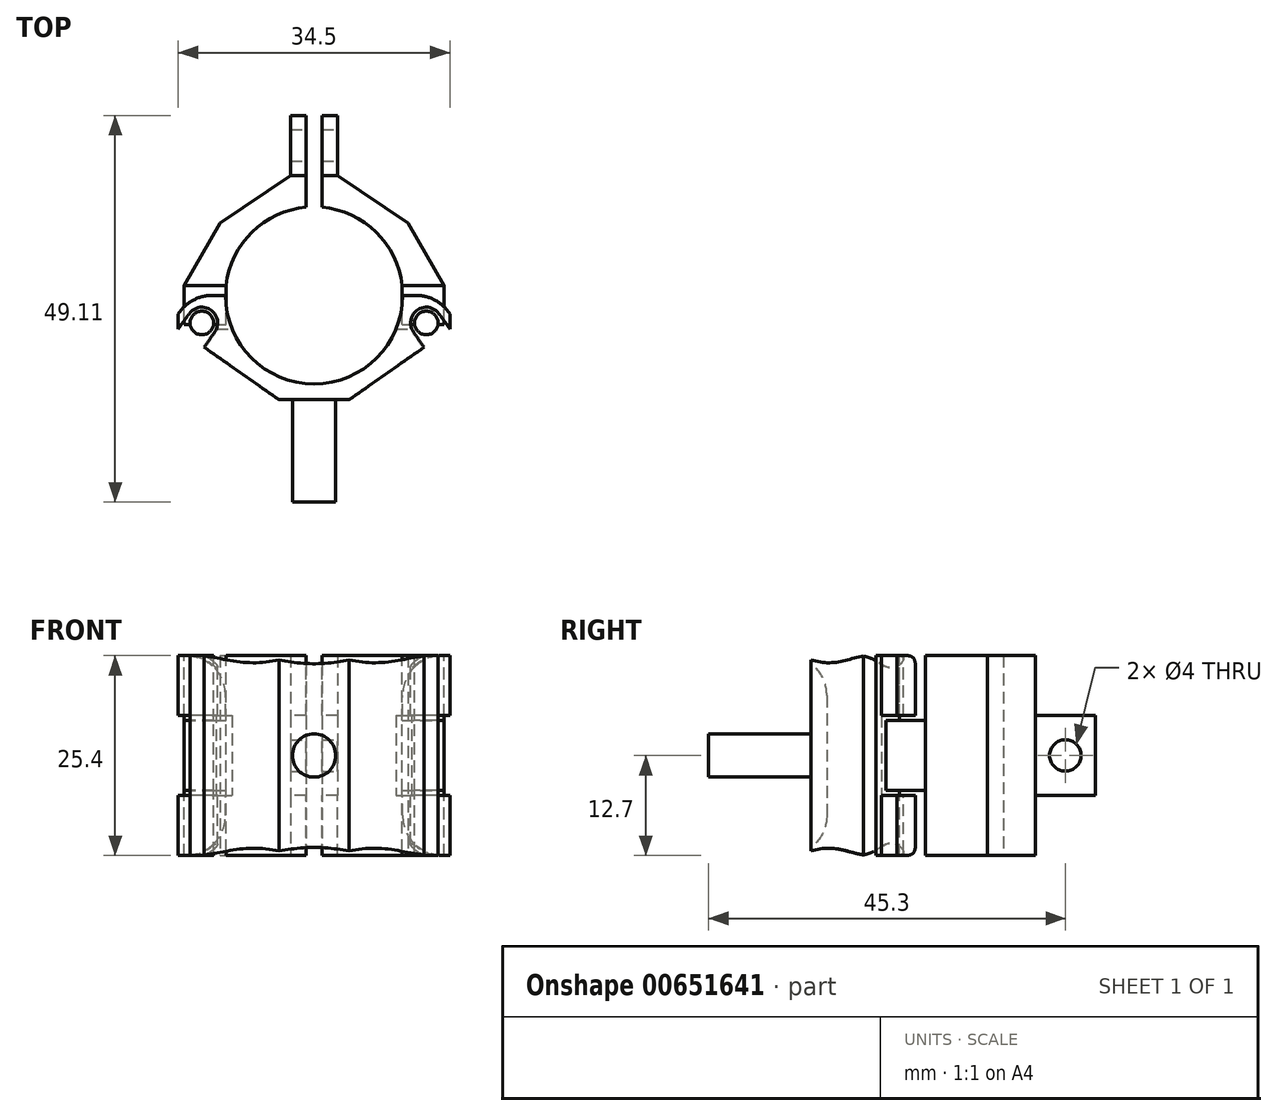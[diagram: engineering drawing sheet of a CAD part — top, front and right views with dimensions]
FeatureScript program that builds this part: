
annotation { "Feature Type Name" : "Feature", "Feature Type Description" : "" }
export const myFeature = defineFeature(function(context is Context, id is Id, definition is map)
    precondition{}
    {
        {
            var Q0;
            Q0=qCreatedBy(makeId("Top.planeOp"),FACE);
            var sketch = newSketch(context, id + "F0", { "sketchPlane" : qUnion([Q0])});
            skCircle(sketch, "E0", {"center": v(0, 0) * mm, "radius": 11.25 * mm});
            skLineSegment(sketch, "E1.bottom", {"start": v(-17.25, 0) * mm, "end": v(17.25, 0) * mm});
            skLineSegment(sketch, "E1.top", {"start": v(-17.25, -13.25) * mm, "end": v(17.25, -13.25) * mm});
            skLineSegment(sketch, "E1.left", {"start": v(-17.25, 0) * mm, "end": v(-17.25, -13.25) * mm});
            skLineSegment(sketch, "E1.right", {"start": v(17.25, 0) * mm, "end": v(17.25, -13.25) * mm});
            skLineSegment(sketch, "E2", {"start": v(-17.25, 0) * mm, "end": v(-11.95, 9.17) * mm});
            skLineSegment(sketch, "E3", {"start": v(-11.95, 9.17) * mm, "end": v(-3, 15.24) * mm});
            skLineSegment(sketch, "E4", {"start": v(17.25, 0) * mm, "end": v(11.95, 9.17) * mm});
            skLineSegment(sketch, "E5", {"start": v(11.95, 9.17) * mm, "end": v(3, 15.24) * mm});
            skLineSegment(sketch, "E6", {"start": v(-3, 15.24) * mm, "end": v(-3, 22.86) * mm});
            skLineSegment(sketch, "E7", {"start": v(-3, 22.86) * mm, "end": v(-1, 22.86) * mm});
            skLineSegment(sketch, "E8", {"start": v(-1, 22.86) * mm, "end": v(-1, 11.2) * mm});
            skLineSegment(sketch, "E9", {"start": v(3, 15.24) * mm, "end": v(3, 22.86) * mm});
            skLineSegment(sketch, "E10", {"start": v(3, 22.86) * mm, "end": v(1, 22.86) * mm});
            skLineSegment(sketch, "E11", {"start": v(1, 22.86) * mm, "end": v(1, 11.2) * mm});
            skSolve(sketch);
        }
        {
            var Q0;
            {var subQ0=sQuery(id+"F0.wireOp",EDGE,"E2");Q0=makeQuery(id+"F0.imprint","IMPRINT",FACE,{"disambiguationData":[TD([[makeQuery(id+"F0.imprint","IMPRINT",EDGE,{"derivedFrom":subQ0}),-1.0]])]});}
            var Q1;
            Q1=makeQuery(id+"F0.imprint","IMPRINT",FACE,{"disambiguationData":[TD([[makeQuery(id+"F0.imprint","IMPRINT",EDGE,{"derivedFrom":sQuery(id+"F0.wireOp",EDGE,"E1.top")}),1.0]])]});
            var Q2;
            {var subQ0=sQuery(id+"F0.wireOp",EDGE,"E4");Q2=makeQuery(id+"F0.imprint","IMPRINT",FACE,{"disambiguationData":[TD([[makeQuery(id+"F0.imprint","IMPRINT",EDGE,{"derivedFrom":subQ0}),1.0]])]});}
            extrude(context, id + "F1", {"entities" : qUnion([Q0, Q1, Q2]), "depth" : 25.4 * mm, "offsetDistance" : 25.4 * mm});
        }
        {
            var Q0;
            Q0=makeQuery(id+"F1.opExtrude","SWEPT_FACE",FACE,{"disambiguationData":[OSD([sQuery(id+"F0.wireOp",EDGE,"E9")])]});
            var sketch = newSketch(context, id + "F2", { "sketchPlane" : qUnion([Q0])});
            skCircle(sketch, "E12", {"center": v(19.05, 12.7) * mm, "radius": 2 * mm});
            skPoint(sketch, "E12.centerSnap0", {"position": v(22.86, 12.7) * mm});
            skPoint(sketch, "E12.centerSnap1", {"position": v(19.05, 25.4) * mm});
            skSolve(sketch);
        }
        {
            var Q0;
            Q0 = qSketchRegion(id + "F2", true);
            extrude(context, id + "F3", {"entities" : qUnion([Q0]), "operationType" : NewBodyOperationType.REMOVE, "oppositeDirection" : true, "depth" : 25.4 * mm, "offsetDistance" : 25.4 * mm});
        }
        {
            var Q0;
            Q0=makeQuery(id+"F1.opExtrude","SWEPT_FACE",FACE,{"disambiguationData":[OSD([sQuery(id+"F0.wireOp",EDGE,"E1.top")])]});
            var sketch = newSketch(context, id + "F4", { "sketchPlane" : qUnion([Q0])});
            skCircle(sketch, "E13", {"center": v(0, 12.7) * mm, "radius": 2.75 * mm});
            skPoint(sketch, "E13.centerSnap0", {"position": v(17.25, 12.7) * mm});
            skSolve(sketch);
        }
        {
            var Q0;
            Q0 = qSketchRegion(id + "F4", true);
            extrude(context, id + "F5", {"entities" : qUnion([Q0]), "operationType" : NewBodyOperationType.ADD, "depth" : 13 * mm, "offsetDistance" : 25.4 * mm});
        }
        {
            var Q0;
            Q0=makeQuery(id+"F1.opExtrude","CAP_FACE",FACE,{"disambiguationData":[OSD([sQuery(id+"F0.wireOp",EDGE,"E0"),sQuery(id+"F0.wireOp",EDGE,"E1.top"),sQuery(id+"F0.wireOp",EDGE,"E1.left"),sQuery(id+"F0.wireOp",EDGE,"E1.right"),sQuery(id+"F0.wireOp",EDGE,"E2"),sQuery(id+"F0.wireOp",EDGE,"E3"),sQuery(id+"F0.wireOp",EDGE,"E4"),sQuery(id+"F0.wireOp",EDGE,"E5"),sQuery(id+"F0.wireOp",EDGE,"E6"),sQuery(id+"F0.wireOp",EDGE,"E7"),sQuery(id+"F0.wireOp",EDGE,"E8"),sQuery(id+"F0.wireOp",EDGE,"E9"),sQuery(id+"F0.wireOp",EDGE,"E10"),sQuery(id+"F0.wireOp",EDGE,"E11")])],"isStart":false});
            var sketch = newSketch(context, id + "F6", { "sketchPlane" : qUnion([Q0])});
            skLineSegment(sketch, "E14", {"start": v(-17.25, 0) * mm, "end": v(-11.25, 0) * mm});
            skCircle(sketch, "E15", {"center": v(-14.25, -3.5) * mm, "radius": 2 * mm});
            skLineSegment(sketch, "E16", {"start": v(11.25, 0) * mm, "end": v(17.25, 0) * mm});
            skCircle(sketch, "E17", {"center": v(14.25, -3.5) * mm, "radius": 2 * mm});
            skLineSegment(sketch, "E18", {"start": v(15.89, -2.35) * mm, "end": v(17.25, -4.3) * mm});
            skLineSegment(sketch, "E19", {"start": v(12.61, -4.65) * mm, "end": v(17.25, -11.27) * mm});
            skLineSegment(sketch, "E20", {"start": v(-12.61, -4.65) * mm, "end": v(-17.25, -11.27) * mm});
            skLineSegment(sketch, "E21", {"start": v(-15.89, -2.35) * mm, "end": v(-17.25, -4.3) * mm});
            skPoint(sketch, "E22", {"position": v(-14.25, 0) * mm});
            skPoint(sketch, "E23", {"position": v(14.25, 0) * mm});
            skSolve(sketch);
        }
        {
            var Q0;
            {var subQ0=sQuery(id+"F6.wireOp",EDGE,"E15");var subQ1=makeQuery(id+"F6.imprint","INTERSECT",VERTEX,{"derivedFrom":[subQ0,sQuery(id+"F6.wireOp",EDGE,"E20")]});Q0=makeQuery(id+"F6.imprint","IMPRINT",FACE,{"disambiguationData":[TD([[makeQuery(id+"F6.imprint","IMPRINT",EDGE,{"disambiguationData":[TD([[subQ1,1.0]])],"derivedFrom":subQ0}),1.0]])]});}
            var Q1;
            {var subQ0=sQuery(id+"F6.wireOp",EDGE,"E20");Q1=makeQuery(id+"F6.imprint","IMPRINT",FACE,{"disambiguationData":[TD([[makeQuery(id+"F6.imprint","IMPRINT",EDGE,{"derivedFrom":subQ0}),-1.0]])]});}
            var Q2;
            {var subQ0=sQuery(id+"F6.wireOp",EDGE,"E17");var subQ1=makeQuery(id+"F6.imprint","INTERSECT",VERTEX,{"derivedFrom":[subQ0,sQuery(id+"F6.wireOp",EDGE,"E18")]});Q2=makeQuery(id+"F6.imprint","IMPRINT",FACE,{"disambiguationData":[TD([[makeQuery(id+"F6.imprint","IMPRINT",EDGE,{"disambiguationData":[TD([[subQ1,-1.0]])],"derivedFrom":subQ0}),1.0]])]});}
            var Q3;
            {var subQ0=sQuery(id+"F6.wireOp",EDGE,"E18");Q3=makeQuery(id+"F6.imprint","IMPRINT",FACE,{"disambiguationData":[TD([[makeQuery(id+"F6.imprint","IMPRINT",EDGE,{"derivedFrom":subQ0}),-1.0]])]});}
            var Q4;
            Q4=makeQuery(id+"F1.opExtrude","CAP_FACE",FACE,{"disambiguationData":[OSD([sQuery(id+"F0.wireOp",EDGE,"E0"),sQuery(id+"F0.wireOp",EDGE,"E1.top"),sQuery(id+"F0.wireOp",EDGE,"E1.left"),sQuery(id+"F0.wireOp",EDGE,"E1.right"),sQuery(id+"F0.wireOp",EDGE,"E2"),sQuery(id+"F0.wireOp",EDGE,"E3"),sQuery(id+"F0.wireOp",EDGE,"E4"),sQuery(id+"F0.wireOp",EDGE,"E5"),sQuery(id+"F0.wireOp",EDGE,"E6"),sQuery(id+"F0.wireOp",EDGE,"E7"),sQuery(id+"F0.wireOp",EDGE,"E8"),sQuery(id+"F0.wireOp",EDGE,"E9"),sQuery(id+"F0.wireOp",EDGE,"E10"),sQuery(id+"F0.wireOp",EDGE,"E11")])],"isStart":true});
            extrude(context, id + "F7", {"entities" : qUnion([Q0, Q1, Q2, Q3]), "operationType" : NewBodyOperationType.REMOVE, "endBound" : BoundingType.UP_TO_SURFACE, "oppositeDirection" : true, "depth" : 50.8 * mm, "endBoundEntityFace" : qUnion([Q4]), "offsetDistance" : 25.4 * mm});
        }
        {
            var Q0;
            {var subQ7=sQuery(id+"F0.wireOp",EDGE,"E4");var subQ10=sQuery(id+"F0.wireOp",EDGE,"E1.right");Q0=makeQuery(id+"F7.boolean.opBoolean","SPLIT",FACE,{"disambiguationData":[TD([makeQuery(id+"F1.opExtrude","SWEPT_FACE",FACE,{"disambiguationData":[OSD([subQ7])]})])],"derivedFrom":makeQuery(id+"F1.opExtrude","SWEPT_FACE",FACE,{"disambiguationData":[OSD([subQ10])]})});}
            var sketch = newSketch(context, id + "F8", { "sketchPlane" : qUnion([Q0])});
            skLineSegment(sketch, "E24.bottom", {"start": v(0, 17.78) * mm, "end": v(-4.3, 17.78) * mm});
            skLineSegment(sketch, "E24.top", {"start": v(0, 7.62) * mm, "end": v(-4.3, 7.62) * mm});
            skLineSegment(sketch, "E24.left", {"start": v(0, 17.78) * mm, "end": v(0, 7.62) * mm});
            skLineSegment(sketch, "E24.right", {"start": v(-4.3, 17.78) * mm, "end": v(-4.3, 7.62) * mm});
            skSolve(sketch);
        }
        {
            var Q0;
            Q0 = qSketchRegion(id + "F8", true);
            var Q1;
            {var subQ9=sQuery(id+"F0.wireOp",EDGE,"E2");var subQ11=sQuery(id+"F0.wireOp",EDGE,"E1.left");Q1=makeQuery(id+"F7.boolean.opBoolean","SPLIT",FACE,{"disambiguationData":[TD([makeQuery(id+"F1.opExtrude","SWEPT_FACE",FACE,{"disambiguationData":[OSD([subQ9])]})])],"derivedFrom":makeQuery(id+"F1.opExtrude","SWEPT_FACE",FACE,{"disambiguationData":[OSD([subQ11])]})});}
            extrude(context, id + "F9", {"entities" : qUnion([Q0]), "operationType" : NewBodyOperationType.REMOVE, "endBound" : BoundingType.UP_TO_SURFACE, "oppositeDirection" : true, "depth" : 25.4 * mm, "endBoundEntityFace" : qUnion([Q1]), "offsetDistance" : 25.4 * mm});
        }
        {
            var Q0;
            Q0=makeQuery(id+"F1.opExtrude","CAP_FACE",FACE,{"disambiguationData":[OSD([sQuery(id+"F0.wireOp",EDGE,"E0"),sQuery(id+"F0.wireOp",EDGE,"E1.top"),sQuery(id+"F0.wireOp",EDGE,"E1.left"),sQuery(id+"F0.wireOp",EDGE,"E1.right"),sQuery(id+"F0.wireOp",EDGE,"E2"),sQuery(id+"F0.wireOp",EDGE,"E3"),sQuery(id+"F0.wireOp",EDGE,"E4"),sQuery(id+"F0.wireOp",EDGE,"E5"),sQuery(id+"F0.wireOp",EDGE,"E6"),sQuery(id+"F0.wireOp",EDGE,"E7"),sQuery(id+"F0.wireOp",EDGE,"E8"),sQuery(id+"F0.wireOp",EDGE,"E9"),sQuery(id+"F0.wireOp",EDGE,"E10"),sQuery(id+"F0.wireOp",EDGE,"E11")])],"isStart":false});
            var sketch = newSketch(context, id + "F10", { "sketchPlane" : qUnion([Q0])});
            skLineSegment(sketch, "E25", {"start": v(-17.25, -2.35) * mm, "end": v(-15.6, 0) * mm});
            skLineSegment(sketch, "E26", {"start": v(17.25, -2.35) * mm, "end": v(15.6, 0) * mm});
            skLineSegment(sketch, "E27", {"start": v(-15.6, 0) * mm, "end": v(15.6, 0) * mm});
            skLineSegment(sketch, "E28", {"start": v(-16.52, 1.27) * mm, "end": v(16.52, 1.27) * mm});
            skSolve(sketch);
        }
        {
            var Q0;
            {var subQ11=sQuery(id+"F10.wireOp",EDGE,"E25");Q0=makeQuery(id+"F10.imprint","IMPRINT",FACE,{"disambiguationData":[TD([[makeQuery(id+"F10.imprint","IMPRINT",EDGE,{"derivedFrom":subQ11}),1.0]])]});}
            var Q1;
            {var subQ11=sQuery(id+"F10.wireOp",EDGE,"E26");Q1=makeQuery(id+"F10.imprint","IMPRINT",FACE,{"disambiguationData":[TD([[makeQuery(id+"F10.imprint","IMPRINT",EDGE,{"derivedFrom":subQ11}),-1.0]])]});}
            var Q2;
            Q2=makeQuery(id+"F1.opExtrude","CAP_FACE",FACE,{"disambiguationData":[OSD([sQuery(id+"F0.wireOp",EDGE,"E0"),sQuery(id+"F0.wireOp",EDGE,"E1.top"),sQuery(id+"F0.wireOp",EDGE,"E1.left"),sQuery(id+"F0.wireOp",EDGE,"E1.right"),sQuery(id+"F0.wireOp",EDGE,"E2"),sQuery(id+"F0.wireOp",EDGE,"E3"),sQuery(id+"F0.wireOp",EDGE,"E4"),sQuery(id+"F0.wireOp",EDGE,"E5"),sQuery(id+"F0.wireOp",EDGE,"E6"),sQuery(id+"F0.wireOp",EDGE,"E7"),sQuery(id+"F0.wireOp",EDGE,"E8"),sQuery(id+"F0.wireOp",EDGE,"E9"),sQuery(id+"F0.wireOp",EDGE,"E10"),sQuery(id+"F0.wireOp",EDGE,"E11")])],"isStart":true});
            extrude(context, id + "F11", {"entities" : qUnion([Q0, Q1]), "operationType" : NewBodyOperationType.REMOVE, "endBound" : BoundingType.UP_TO_SURFACE, "oppositeDirection" : true, "depth" : 25.4 * mm, "endBoundEntityFace" : qUnion([Q2]), "offsetDistance" : 25.4 * mm});
        }
        {
            var Q0;
            {var subQ0=sQuery(id+"F10.wireOp",EDGE,"E28");Q0=makeQuery(id+"F11.boolean.opBoolean","COPY",FACE,{"derivedFrom":makeQuery(id+"F11.opExtrude","SWEPT_FACE",FACE,{"disambiguationData":[OSD([subQ0]),TDD([makeQuery(id+"F10.imprint","IMPRINT",EDGE,{"disambiguationData":[TD([[makeQuery(id+"F10.imprint","INTERSECT",VERTEX,{"derivedFrom":[makeQuery(id+"F1.opExtrude","CAP_EDGE",EDGE,{"disambiguationData":[OSD([sQuery(id+"F0.wireOp",EDGE,"E2")])],"isStart":false}),subQ0]}),-1.0]])],"derivedFrom":subQ0})])]})});}
            var sketch = newSketch(context, id + "F12", { "sketchPlane" : qUnion([Q0])});
            skLineSegment(sketch, "E29.bottom", {"start": v(-16.52, 17.14) * mm, "end": v(-11.18, 17.14) * mm});
            skLineSegment(sketch, "E29.top", {"start": v(-16.52, 8.26) * mm, "end": v(-11.18, 8.26) * mm});
            skLineSegment(sketch, "E29.left", {"start": v(-16.52, 17.14) * mm, "end": v(-16.52, 8.26) * mm});
            skLineSegment(sketch, "E29.right", {"start": v(-11.18, 17.14) * mm, "end": v(-11.18, 8.26) * mm});
            skSolve(sketch);
        }
        {
            var Q0;
            {var subQ0=sQuery(id+"F10.wireOp",EDGE,"E28");Q0=makeQuery(id+"F11.boolean.opBoolean","COPY",FACE,{"derivedFrom":makeQuery(id+"F11.opExtrude","SWEPT_FACE",FACE,{"disambiguationData":[OSD([subQ0]),TDD([makeQuery(id+"F10.imprint","IMPRINT",EDGE,{"disambiguationData":[TD([[makeQuery(id+"F10.imprint","INTERSECT",VERTEX,{"derivedFrom":[makeQuery(id+"F1.opExtrude","CAP_EDGE",EDGE,{"disambiguationData":[OSD([sQuery(id+"F0.wireOp",EDGE,"E4")])],"isStart":false}),subQ0]}),1.0]])],"derivedFrom":subQ0})])]})});}
            var sketch = newSketch(context, id + "F13", { "sketchPlane" : qUnion([Q0])});
            skLineSegment(sketch, "E30", {"start": v(11.18, 17.14) * mm, "end": v(16.52, 17.14) * mm});
            skLineSegment(sketch, "E31", {"start": v(11.18, 8.26) * mm, "end": v(16.52, 8.26) * mm});
            skLineSegment(sketch, "E32", {"start": v(11.18, 17.14) * mm, "end": v(11.18, 8.26) * mm});
            skLineSegment(sketch, "E33", {"start": v(16.52, 17.14) * mm, "end": v(16.52, 8.26) * mm});
            skSolve(sketch);
        }
        {
            var Q0;
            Q0 = qSketchRegion(id + "F13", true);
            var Q1;
            Q1 = qSketchRegion(id + "F12", true);
            var Q2;
            Q2=makeQuery(id+"F11.boolean.opBoolean","SPLIT",BODY,{"disambiguationData":[OD(2.0)],"derivedFrom":makeQuery(id+"F1.opExtrude","SWEPT_BODY",BODY,{"disambiguationData":[OSD([sQuery(id+"F0.wireOp",EDGE,"E0"),sQuery(id+"F0.wireOp",EDGE,"E1.top"),sQuery(id+"F0.wireOp",EDGE,"E1.left"),sQuery(id+"F0.wireOp",EDGE,"E1.right"),sQuery(id+"F0.wireOp",EDGE,"E2"),sQuery(id+"F0.wireOp",EDGE,"E3"),sQuery(id+"F0.wireOp",EDGE,"E4"),sQuery(id+"F0.wireOp",EDGE,"E5"),sQuery(id+"F0.wireOp",EDGE,"E6"),sQuery(id+"F0.wireOp",EDGE,"E7"),sQuery(id+"F0.wireOp",EDGE,"E8"),sQuery(id+"F0.wireOp",EDGE,"E9"),sQuery(id+"F0.wireOp",EDGE,"E10"),sQuery(id+"F0.wireOp",EDGE,"E11")])]})});
            extrude(context, id + "F14", {"entities" : qUnion([Q0, Q1]), "operationType" : NewBodyOperationType.ADD, "depth" : 5 * mm, "endBoundEntityBody" : qUnion([Q2]), "offsetDistance" : 25.4 * mm});
        }
        {
            var Q0;
            {var subQ0=sQuery(id+"F0.wireOp",EDGE,"E0");var subQ1=sQuery(id+"F0.wireOp",EDGE,"E1.right");var subQ2=sQuery(id+"F0.wireOp",EDGE,"E1.top");var subQ3=sQuery(id+"F0.wireOp",EDGE,"E1.left");Q0=makeQuery(id+"F11.boolean.opBoolean","SPLIT",FACE,{"disambiguationData":[TD([makeQuery(id+"F1.opExtrude","SWEPT_FACE",FACE,{"disambiguationData":[OSD([subQ2])]})])],"derivedFrom":makeQuery(id+"F1.opExtrude","CAP_FACE",FACE,{"disambiguationData":[OSD([subQ0,subQ2,subQ3,subQ1,sQuery(id+"F0.wireOp",EDGE,"E2"),sQuery(id+"F0.wireOp",EDGE,"E3"),sQuery(id+"F0.wireOp",EDGE,"E4"),sQuery(id+"F0.wireOp",EDGE,"E5"),sQuery(id+"F0.wireOp",EDGE,"E6"),sQuery(id+"F0.wireOp",EDGE,"E7"),sQuery(id+"F0.wireOp",EDGE,"E8"),sQuery(id+"F0.wireOp",EDGE,"E9"),sQuery(id+"F0.wireOp",EDGE,"E10"),sQuery(id+"F0.wireOp",EDGE,"E11")])],"isStart":false})});}
            var sketch = newSketch(context, id + "F15", { "sketchPlane" : qUnion([Q0])});
            skCircle(sketch, "E34", {"center": v(-14.25, -3.5) * mm, "radius": 1.5 * mm});
            skCircle(sketch, "E35", {"center": v(14.25, -3.5) * mm, "radius": 1.5 * mm});
            skSolve(sketch);
        }
        {
            var Q0;
            Q0 = qSketchRegion(id + "F15", true);
            var Q1;
            {var subQ0=sQuery(id+"F0.wireOp",EDGE,"E0");var subQ1=sQuery(id+"F0.wireOp",EDGE,"E1.right");var subQ2=sQuery(id+"F0.wireOp",EDGE,"E1.top");var subQ3=sQuery(id+"F0.wireOp",EDGE,"E1.left");Q1=makeQuery(id+"F11.boolean.opBoolean","SPLIT",FACE,{"disambiguationData":[TD([makeQuery(id+"F1.opExtrude","SWEPT_FACE",FACE,{"disambiguationData":[OSD([subQ2])]})])],"derivedFrom":makeQuery(id+"F1.opExtrude","CAP_FACE",FACE,{"disambiguationData":[OSD([subQ0,subQ2,subQ3,subQ1,sQuery(id+"F0.wireOp",EDGE,"E2"),sQuery(id+"F0.wireOp",EDGE,"E3"),sQuery(id+"F0.wireOp",EDGE,"E4"),sQuery(id+"F0.wireOp",EDGE,"E5"),sQuery(id+"F0.wireOp",EDGE,"E6"),sQuery(id+"F0.wireOp",EDGE,"E7"),sQuery(id+"F0.wireOp",EDGE,"E8"),sQuery(id+"F0.wireOp",EDGE,"E9"),sQuery(id+"F0.wireOp",EDGE,"E10"),sQuery(id+"F0.wireOp",EDGE,"E11")])],"isStart":true})});}
            extrude(context, id + "F16", {"entities" : qUnion([Q0]), "operationType" : NewBodyOperationType.ADD, "endBound" : BoundingType.UP_TO_SURFACE, "oppositeDirection" : true, "depth" : 25.4 * mm, "endBoundEntityFace" : qUnion([Q1]), "offsetDistance" : 25.4 * mm});
        }
        {
            var Q0;
            {var subQ0=sQuery(id+"F0.wireOp",EDGE,"E0");var subQ1=sQuery(id+"F0.wireOp",EDGE,"E1.right");var subQ2=sQuery(id+"F0.wireOp",EDGE,"E1.top");var subQ3=sQuery(id+"F0.wireOp",EDGE,"E1.left");Q0=makeQuery(id+"F11.boolean.opBoolean","SPLIT",FACE,{"disambiguationData":[TD([makeQuery(id+"F1.opExtrude","SWEPT_FACE",FACE,{"disambiguationData":[OSD([subQ2])]})])],"derivedFrom":makeQuery(id+"F1.opExtrude","CAP_FACE",FACE,{"disambiguationData":[OSD([subQ0,subQ2,subQ3,subQ1,sQuery(id+"F0.wireOp",EDGE,"E2"),sQuery(id+"F0.wireOp",EDGE,"E3"),sQuery(id+"F0.wireOp",EDGE,"E4"),sQuery(id+"F0.wireOp",EDGE,"E5"),sQuery(id+"F0.wireOp",EDGE,"E6"),sQuery(id+"F0.wireOp",EDGE,"E7"),sQuery(id+"F0.wireOp",EDGE,"E8"),sQuery(id+"F0.wireOp",EDGE,"E9"),sQuery(id+"F0.wireOp",EDGE,"E10"),sQuery(id+"F0.wireOp",EDGE,"E11")])],"isStart":false})});}
            var sketch = newSketch(context, id + "F17", { "sketchPlane" : qUnion([Q0])});
            skLineSegment(sketch, "E36", {"start": v(-17.25, -4.3) * mm, "end": v(-4.46, -13.25) * mm});
            skLineSegment(sketch, "E37", {"start": v(17.25, -4.3) * mm, "end": v(4.46, -13.25) * mm});
            skSolve(sketch);
        }
        {
            var Q0;
            Q0 = qSketchRegion(id + "F17", true);
            var Q1;
            {var subQ0=sQuery(id+"F17.wireOp",EDGE,"E36");var subQ1=sQuery(id+"F0.wireOp",EDGE,"E1.top");var subQ2=makeQuery(id+"F1.opExtrude","CAP_EDGE",EDGE,{"disambiguationData":[OSD([subQ1])],"isStart":false});var subQ3=makeQuery(id+"F17.imprint","INTERSECT",VERTEX,{"derivedFrom":[subQ2,subQ0]});Q1=makeQuery(id+"F17.imprint","IMPRINT",FACE,{"disambiguationData":[TD([[makeQuery(id+"F17.imprint","IMPRINT",EDGE,{"disambiguationData":[TD([[subQ3,1.0]])],"derivedFrom":subQ0}),-1.0]])]});}
            var Q2;
            {var subQ0=sQuery(id+"F17.wireOp",EDGE,"E37");var subQ1=sQuery(id+"F0.wireOp",EDGE,"E1.top");var subQ2=makeQuery(id+"F1.opExtrude","CAP_EDGE",EDGE,{"disambiguationData":[OSD([subQ1])],"isStart":false});var subQ3=makeQuery(id+"F17.imprint","INTERSECT",VERTEX,{"derivedFrom":[subQ2,subQ0]});Q2=makeQuery(id+"F17.imprint","IMPRINT",FACE,{"disambiguationData":[TD([[makeQuery(id+"F17.imprint","IMPRINT",EDGE,{"disambiguationData":[TD([[subQ3,1.0]])],"derivedFrom":subQ0}),1.0]])]});}
            var Q3;
            {var subQ0=sQuery(id+"F0.wireOp",EDGE,"E0");var subQ1=sQuery(id+"F0.wireOp",EDGE,"E1.right");var subQ2=sQuery(id+"F0.wireOp",EDGE,"E1.top");var subQ3=sQuery(id+"F0.wireOp",EDGE,"E1.left");Q3=makeQuery(id+"F11.boolean.opBoolean","SPLIT",FACE,{"disambiguationData":[TD([makeQuery(id+"F1.opExtrude","SWEPT_FACE",FACE,{"disambiguationData":[OSD([subQ2])]})])],"derivedFrom":makeQuery(id+"F1.opExtrude","CAP_FACE",FACE,{"disambiguationData":[OSD([subQ0,subQ2,subQ3,subQ1,sQuery(id+"F0.wireOp",EDGE,"E2"),sQuery(id+"F0.wireOp",EDGE,"E3"),sQuery(id+"F0.wireOp",EDGE,"E4"),sQuery(id+"F0.wireOp",EDGE,"E5"),sQuery(id+"F0.wireOp",EDGE,"E6"),sQuery(id+"F0.wireOp",EDGE,"E7"),sQuery(id+"F0.wireOp",EDGE,"E8"),sQuery(id+"F0.wireOp",EDGE,"E9"),sQuery(id+"F0.wireOp",EDGE,"E10"),sQuery(id+"F0.wireOp",EDGE,"E11")])],"isStart":true})});}
            extrude(context, id + "F18", {"entities" : qUnion([Q0, Q1, Q2]), "operationType" : NewBodyOperationType.REMOVE, "endBound" : BoundingType.UP_TO_SURFACE, "oppositeDirection" : true, "depth" : 25.4 * mm, "endBoundEntityFace" : qUnion([Q3]), "offsetDistance" : 25.4 * mm});
        }
        {
            var Q0;
            Q0=makeQuery(id+"F1.opExtrude","SWEPT_FACE",FACE,{"disambiguationData":[OSD([sQuery(id+"F0.wireOp",EDGE,"E6")])]});
            var sketch = newSketch(context, id + "F19", { "sketchPlane" : qUnion([Q0])});
            skLineSegment(sketch, "E38.bottom", {"start": v(-22.86, 0) * mm, "end": v(-15.24, 0) * mm});
            skLineSegment(sketch, "E38.top", {"start": v(-22.86, 7.62) * mm, "end": v(-15.24, 7.62) * mm});
            skLineSegment(sketch, "E38.left", {"start": v(-22.86, 0) * mm, "end": v(-22.86, 7.62) * mm});
            skLineSegment(sketch, "E38.right", {"start": v(-15.24, 0) * mm, "end": v(-15.24, 7.62) * mm});
            skLineSegment(sketch, "E39.bottom", {"start": v(-22.86, 25.4) * mm, "end": v(-15.24, 25.4) * mm});
            skLineSegment(sketch, "E39.top", {"start": v(-22.86, 17.78) * mm, "end": v(-15.24, 17.78) * mm});
            skLineSegment(sketch, "E39.left", {"start": v(-22.86, 25.4) * mm, "end": v(-22.86, 17.78) * mm});
            skLineSegment(sketch, "E39.right", {"start": v(-15.24, 25.4) * mm, "end": v(-15.24, 17.78) * mm});
            skSolve(sketch);
        }
        {
            var Q0;
            Q0=makeQuery(id+"F19.imprint","IMPRINT",FACE,{"disambiguationData":[TD([[makeQuery(id+"F19.imprint","IMPRINT",EDGE,{"derivedFrom":sQuery(id+"F19.wireOp",EDGE,"E38.bottom")}),-1.0]])]});
            var Q1;
            Q1=makeQuery(id+"F19.imprint","IMPRINT",FACE,{"disambiguationData":[TD([[makeQuery(id+"F19.imprint","IMPRINT",EDGE,{"derivedFrom":sQuery(id+"F19.wireOp",EDGE,"E39.bottom")}),1.0]])]});
            var Q2;
            Q2=makeQuery(id+"F1.opExtrude","SWEPT_FACE",FACE,{"disambiguationData":[OSD([sQuery(id+"F0.wireOp",EDGE,"E9")])]});
            extrude(context, id + "F20", {"entities" : qUnion([Q0, Q1]), "operationType" : NewBodyOperationType.REMOVE, "endBound" : BoundingType.UP_TO_SURFACE, "oppositeDirection" : true, "depth" : 25.4 * mm, "endBoundEntityFace" : qUnion([Q2]), "offsetDistance" : 25.4 * mm});
        }
        {
            var Q0;
            {var subQ0=sQuery(id+"F0.wireOp",EDGE,"E7");var subQ1=sQuery(id+"F19.wireOp",EDGE,"E39.top");Q0=makeQuery(id+"F20.boolean.opBoolean","COPY",EDGE,{"disambiguationData":[topologyDisambiguationEdgeConnected([makeQuery(id+"F1.opExtrude","SWEPT_FACE",FACE,{"disambiguationData":[OSD([subQ0])]})])],"derivedFrom":makeQuery(id+"F20.opExtrude","SWEPT_EDGE",EDGE,{"disambiguationData":[OSD([sQuery(id+"F0.wireOp",EDGE,"E6"),subQ0,subQ1,sQuery(id+"F19.wireOp",EDGE,"E39.left")])]})});}
            var Q1;
            {var subQ0=sQuery(id+"F0.wireOp",EDGE,"E7");var subQ1=sQuery(id+"F19.wireOp",EDGE,"E38.top");Q1=makeQuery(id+"F20.boolean.opBoolean","COPY",EDGE,{"disambiguationData":[topologyDisambiguationEdgeConnected([makeQuery(id+"F1.opExtrude","SWEPT_FACE",FACE,{"disambiguationData":[OSD([subQ0])]})])],"derivedFrom":makeQuery(id+"F20.opExtrude","SWEPT_EDGE",EDGE,{"disambiguationData":[OSD([sQuery(id+"F0.wireOp",EDGE,"E6"),subQ0,subQ1,sQuery(id+"F19.wireOp",EDGE,"E38.left")])]})});}
            var Q2;
            {var subQ0=sQuery(id+"F19.wireOp",EDGE,"E38.top");Q2=makeQuery(id+"F20.boolean.opBoolean","COPY",EDGE,{"disambiguationData":[topologyDisambiguationEdgeConnected([makeQuery(id+"F1.opExtrude","SWEPT_FACE",FACE,{"disambiguationData":[OSD([sQuery(id+"F0.wireOp",EDGE,"E10")])]})])],"derivedFrom":makeQuery(id+"F20.opExtrude","SWEPT_EDGE",EDGE,{"disambiguationData":[OSD([sQuery(id+"F0.wireOp",EDGE,"E6"),sQuery(id+"F0.wireOp",EDGE,"E7"),subQ0,sQuery(id+"F19.wireOp",EDGE,"E38.left")])]})});}
            var Q3;
            {var subQ0=sQuery(id+"F19.wireOp",EDGE,"E39.top");Q3=makeQuery(id+"F20.boolean.opBoolean","COPY",EDGE,{"disambiguationData":[topologyDisambiguationEdgeConnected([makeQuery(id+"F1.opExtrude","SWEPT_FACE",FACE,{"disambiguationData":[OSD([sQuery(id+"F0.wireOp",EDGE,"E10")])]})])],"derivedFrom":makeQuery(id+"F20.opExtrude","SWEPT_EDGE",EDGE,{"disambiguationData":[OSD([sQuery(id+"F0.wireOp",EDGE,"E6"),sQuery(id+"F0.wireOp",EDGE,"E7"),subQ0,sQuery(id+"F19.wireOp",EDGE,"E39.left")])]})});}
            var Q4;
            {var subQ1=sQuery(id+"F0.wireOp",EDGE,"E3");var subQ2=sQuery(id+"F19.wireOp",EDGE,"E39.right");Q4=makeQuery(id+"F20.boolean.opBoolean","COPY",EDGE,{"disambiguationData":[TD([makeQuery(id+"F1.opExtrude","SWEPT_FACE",FACE,{"disambiguationData":[OSD([subQ1])]})])],"derivedFrom":makeQuery(id+"F20.opExtrude","SWEPT_EDGE",EDGE,{"disambiguationData":[OSD([sQuery(id+"F19.wireOp",EDGE,"E39.bottom"),subQ2])]})});}
            var Q5;
            {var subQ1=sQuery(id+"F0.wireOp",EDGE,"E5");var subQ2=sQuery(id+"F19.wireOp",EDGE,"E39.right");Q5=makeQuery(id+"F20.boolean.opBoolean","COPY",EDGE,{"disambiguationData":[TD([makeQuery(id+"F1.opExtrude","SWEPT_FACE",FACE,{"disambiguationData":[OSD([subQ1])]})])],"derivedFrom":makeQuery(id+"F20.opExtrude","SWEPT_EDGE",EDGE,{"disambiguationData":[OSD([sQuery(id+"F19.wireOp",EDGE,"E39.bottom"),subQ2])]})});}
            var Q6;
            {var subQ1=sQuery(id+"F0.wireOp",EDGE,"E3");var subQ2=sQuery(id+"F19.wireOp",EDGE,"E38.right");Q6=makeQuery(id+"F20.boolean.opBoolean","COPY",EDGE,{"disambiguationData":[TD([makeQuery(id+"F1.opExtrude","SWEPT_FACE",FACE,{"disambiguationData":[OSD([subQ1])]})])],"derivedFrom":makeQuery(id+"F20.opExtrude","SWEPT_EDGE",EDGE,{"disambiguationData":[OSD([sQuery(id+"F19.wireOp",EDGE,"E38.bottom"),subQ2])]})});}
            var Q7;
            {var subQ1=sQuery(id+"F0.wireOp",EDGE,"E5");var subQ2=sQuery(id+"F19.wireOp",EDGE,"E38.right");Q7=makeQuery(id+"F20.boolean.opBoolean","COPY",EDGE,{"disambiguationData":[TD([makeQuery(id+"F1.opExtrude","SWEPT_FACE",FACE,{"disambiguationData":[OSD([subQ1])]})])],"derivedFrom":makeQuery(id+"F20.opExtrude","SWEPT_EDGE",EDGE,{"disambiguationData":[OSD([sQuery(id+"F19.wireOp",EDGE,"E38.bottom"),subQ2])]})});}
            var Q8;
            Q8=makeQuery(id+"F18.boolean.opBoolean","COPY",EDGE,{"derivedFrom":makeQuery(id+"F18.opExtrude","SWEPT_EDGE",EDGE,{"disambiguationData":[OSD([sQuery(id+"F6.wireOp",EDGE,"E20"),sQuery(id+"F17.wireOp",EDGE,"E36")])]})});
            var Q9;
            Q9=makeQuery(id+"F18.boolean.opBoolean","COPY",EDGE,{"derivedFrom":makeQuery(id+"F18.opExtrude","SWEPT_EDGE",EDGE,{"disambiguationData":[OSD([sQuery(id+"F6.wireOp",EDGE,"E19"),sQuery(id+"F17.wireOp",EDGE,"E37")])]})});
            var Q10;
            Q10=makeQuery(id+"F1.opExtrude","SWEPT_EDGE",EDGE,{"disambiguationData":[OSD([sQuery(id+"F0.wireOp",EDGE,"E2"),sQuery(id+"F0.wireOp",EDGE,"E3")])]});
            var Q11;
            Q11=makeQuery(id+"F1.opExtrude","SWEPT_EDGE",EDGE,{"disambiguationData":[OSD([sQuery(id+"F0.wireOp",EDGE,"E4"),sQuery(id+"F0.wireOp",EDGE,"E5")])]});
            var Q12;
            {var subQ1=sQuery(id+"F0.wireOp",EDGE,"E1.right");var subQ3=sQuery(id+"F10.wireOp",EDGE,"E26");var subQ4=sQuery(id+"F10.wireOp",EDGE,"E27");Q12=makeQuery(id+"F11.boolean.opBoolean","COPY",EDGE,{"disambiguationData":[TD([makeQuery(id+"F9.boolean.opBoolean","COPY",FACE,{"disambiguationData":[TD([makeQuery(id+"F1.opExtrude","SWEPT_FACE",FACE,{"disambiguationData":[OSD([subQ1])]})])],"derivedFrom":makeQuery(id+"F9.opExtrude","SWEPT_FACE",FACE,{"disambiguationData":[OSD([sQuery(id+"F8.wireOp",EDGE,"E24.bottom")])]})})])],"derivedFrom":makeQuery(id+"F11.opExtrude","SWEPT_EDGE",EDGE,{"disambiguationData":[OSD([subQ3,subQ4])]})});}
            var Q13;
            {var subQ1=sQuery(id+"F0.wireOp",EDGE,"E1.right");var subQ3=sQuery(id+"F10.wireOp",EDGE,"E26");var subQ4=sQuery(id+"F10.wireOp",EDGE,"E27");Q13=makeQuery(id+"F11.boolean.opBoolean","COPY",EDGE,{"disambiguationData":[TD([makeQuery(id+"F9.boolean.opBoolean","COPY",FACE,{"disambiguationData":[TD([makeQuery(id+"F1.opExtrude","SWEPT_FACE",FACE,{"disambiguationData":[OSD([subQ1])]})])],"derivedFrom":makeQuery(id+"F9.opExtrude","SWEPT_FACE",FACE,{"disambiguationData":[OSD([sQuery(id+"F8.wireOp",EDGE,"E24.top")])]})})])],"derivedFrom":makeQuery(id+"F11.opExtrude","SWEPT_EDGE",EDGE,{"disambiguationData":[OSD([subQ3,subQ4])]})});}
            var Q14;
            {var subQ1=sQuery(id+"F0.wireOp",EDGE,"E1.left");var subQ3=sQuery(id+"F10.wireOp",EDGE,"E27");var subQ4=sQuery(id+"F10.wireOp",EDGE,"E25");Q14=makeQuery(id+"F11.boolean.opBoolean","COPY",EDGE,{"disambiguationData":[TD([makeQuery(id+"F9.boolean.opBoolean","COPY",FACE,{"disambiguationData":[TD([makeQuery(id+"F1.opExtrude","SWEPT_FACE",FACE,{"disambiguationData":[OSD([subQ1])]})])],"derivedFrom":makeQuery(id+"F9.opExtrude","SWEPT_FACE",FACE,{"disambiguationData":[OSD([sQuery(id+"F8.wireOp",EDGE,"E24.bottom")])]})})])],"derivedFrom":makeQuery(id+"F11.opExtrude","SWEPT_EDGE",EDGE,{"disambiguationData":[OSD([subQ4,subQ3])]})});}
            var Q15;
            {var subQ1=sQuery(id+"F0.wireOp",EDGE,"E1.left");var subQ3=sQuery(id+"F10.wireOp",EDGE,"E25");var subQ4=sQuery(id+"F10.wireOp",EDGE,"E27");Q15=makeQuery(id+"F11.boolean.opBoolean","COPY",EDGE,{"disambiguationData":[TD([makeQuery(id+"F9.boolean.opBoolean","COPY",FACE,{"disambiguationData":[TD([makeQuery(id+"F1.opExtrude","SWEPT_FACE",FACE,{"disambiguationData":[OSD([subQ1])]})])],"derivedFrom":makeQuery(id+"F9.opExtrude","SWEPT_FACE",FACE,{"disambiguationData":[OSD([sQuery(id+"F8.wireOp",EDGE,"E24.top")])]})})])],"derivedFrom":makeQuery(id+"F11.opExtrude","SWEPT_EDGE",EDGE,{"disambiguationData":[OSD([subQ3,subQ4])]})});}
            var Q16;
            {var subQ1=sQuery(id+"F0.wireOp",EDGE,"E1.left");var subQ3=makeQuery(id+"F1.opExtrude","SWEPT_FACE",FACE,{"disambiguationData":[OSD([subQ1])]});var subQ4=sQuery(id+"F10.wireOp",EDGE,"E25");Q16=makeQuery(id+"F11.boolean.opBoolean","COPY",EDGE,{"disambiguationData":[TD([makeQuery(id+"F9.boolean.opBoolean","COPY",FACE,{"disambiguationData":[TD([subQ3])],"derivedFrom":makeQuery(id+"F9.opExtrude","SWEPT_FACE",FACE,{"disambiguationData":[OSD([sQuery(id+"F8.wireOp",EDGE,"E24.bottom")])]})})])],"derivedFrom":makeQuery(id+"F11.opExtrude","SWEPT_EDGE",EDGE,{"disambiguationData":[OSD([subQ1,subQ4])]})});}
            var Q17;
            {var subQ1=sQuery(id+"F0.wireOp",EDGE,"E1.left");var subQ3=makeQuery(id+"F1.opExtrude","SWEPT_FACE",FACE,{"disambiguationData":[OSD([subQ1])]});var subQ4=sQuery(id+"F10.wireOp",EDGE,"E25");Q17=makeQuery(id+"F11.boolean.opBoolean","COPY",EDGE,{"disambiguationData":[TD([makeQuery(id+"F9.boolean.opBoolean","COPY",FACE,{"disambiguationData":[TD([subQ3])],"derivedFrom":makeQuery(id+"F9.opExtrude","SWEPT_FACE",FACE,{"disambiguationData":[OSD([sQuery(id+"F8.wireOp",EDGE,"E24.top")])]})})])],"derivedFrom":makeQuery(id+"F11.opExtrude","SWEPT_EDGE",EDGE,{"disambiguationData":[OSD([subQ1,subQ4])]})});}
            var Q18;
            {var subQ1=sQuery(id+"F0.wireOp",EDGE,"E1.right");var subQ3=sQuery(id+"F10.wireOp",EDGE,"E26");var subQ4=makeQuery(id+"F1.opExtrude","SWEPT_FACE",FACE,{"disambiguationData":[OSD([subQ1])]});Q18=makeQuery(id+"F11.boolean.opBoolean","COPY",EDGE,{"disambiguationData":[TD([makeQuery(id+"F9.boolean.opBoolean","COPY",FACE,{"disambiguationData":[TD([subQ4])],"derivedFrom":makeQuery(id+"F9.opExtrude","SWEPT_FACE",FACE,{"disambiguationData":[OSD([sQuery(id+"F8.wireOp",EDGE,"E24.top")])]})})])],"derivedFrom":makeQuery(id+"F11.opExtrude","SWEPT_EDGE",EDGE,{"disambiguationData":[OSD([subQ1,subQ3])]})});}
            var Q19;
            Q19=makeQuery(id+"F18.boolean.opBoolean","COPY",EDGE,{"derivedFrom":makeQuery(id+"F18.opExtrude","SWEPT_EDGE",EDGE,{"disambiguationData":[OSD([sQuery(id+"F0.wireOp",EDGE,"E1.top"),sQuery(id+"F17.wireOp",EDGE,"E37")])]})});
            var Q20;
            Q20=makeQuery(id+"F18.boolean.opBoolean","COPY",EDGE,{"derivedFrom":makeQuery(id+"F18.opExtrude","SWEPT_EDGE",EDGE,{"disambiguationData":[OSD([sQuery(id+"F0.wireOp",EDGE,"E1.top"),sQuery(id+"F17.wireOp",EDGE,"E36")])]})});
            var Q21;
            {var subQ1=sQuery(id+"F0.wireOp",EDGE,"E1.right");var subQ3=makeQuery(id+"F1.opExtrude","SWEPT_FACE",FACE,{"disambiguationData":[OSD([subQ1])]});var subQ4=sQuery(id+"F10.wireOp",EDGE,"E26");Q21=makeQuery(id+"F11.boolean.opBoolean","COPY",EDGE,{"disambiguationData":[TD([makeQuery(id+"F9.boolean.opBoolean","COPY",FACE,{"disambiguationData":[TD([subQ3])],"derivedFrom":makeQuery(id+"F9.opExtrude","SWEPT_FACE",FACE,{"disambiguationData":[OSD([sQuery(id+"F8.wireOp",EDGE,"E24.bottom")])]})})])],"derivedFrom":makeQuery(id+"F11.opExtrude","SWEPT_EDGE",EDGE,{"disambiguationData":[OSD([subQ1,subQ4])]})});}
            var Q22;
            Q22=makeQuery(id+"F14.boolean.opBoolean","MERGE",EDGE,{"derivedFrom":[makeQuery(id+"F11.boolean.opBoolean","COPY",EDGE,{"derivedFrom":makeQuery(id+"F11.opExtrude","SWEPT_EDGE",EDGE,{"disambiguationData":[OSD([sQuery(id+"F0.wireOp",EDGE,"E2"),sQuery(id+"F10.wireOp",EDGE,"E28")])]})}),makeQuery(id+"F14.opExtrude","CAP_EDGE",EDGE,{"disambiguationData":[OSD([sQuery(id+"F12.wireOp",EDGE,"E29.left")])],"isStart":true})]});
            var Q23;
            Q23=makeQuery(id+"F14.boolean.opBoolean","MERGE",EDGE,{"derivedFrom":[makeQuery(id+"F11.boolean.opBoolean","COPY",EDGE,{"derivedFrom":makeQuery(id+"F11.opExtrude","SWEPT_EDGE",EDGE,{"disambiguationData":[OSD([sQuery(id+"F0.wireOp",EDGE,"E4"),sQuery(id+"F10.wireOp",EDGE,"E28")])]})}),makeQuery(id+"F14.opExtrude","CAP_EDGE",EDGE,{"disambiguationData":[OSD([sQuery(id+"F13.wireOp",EDGE,"E33")])],"isStart":true})]});
            var Q24;
            Q24=makeQuery(id+"F1.opExtrude","CAP_EDGE",EDGE,{"disambiguationData":[OSD([sQuery(id+"F0.wireOp",EDGE,"E4")])],"isStart":true});
            var Q25;
            Q25=makeQuery(id+"F1.opExtrude","CAP_EDGE",EDGE,{"disambiguationData":[OSD([sQuery(id+"F0.wireOp",EDGE,"E4")])],"isStart":false});
            var Q26;
            Q26=makeQuery(id+"F1.opExtrude","CAP_EDGE",EDGE,{"disambiguationData":[OSD([sQuery(id+"F0.wireOp",EDGE,"E2")])],"isStart":true});
            var Q27;
            Q27=makeQuery(id+"F1.opExtrude","CAP_EDGE",EDGE,{"disambiguationData":[OSD([sQuery(id+"F0.wireOp",EDGE,"E2")])],"isStart":false});
            var Q28;
            {var subQ0=sQuery(id+"F0.wireOp",EDGE,"E0");var subQ1=sQuery(id+"F10.wireOp",EDGE,"E27");var subQ2=makeQuery(id+"F1.opExtrude","CAP_EDGE",EDGE,{"disambiguationData":[OSD([subQ0])],"isStart":false});Q28=makeQuery(id+"F11.boolean.opBoolean","SPLIT",EDGE,{"disambiguationData":[TD([makeQuery(id+"F11.opExtrude","SWEPT_FACE",FACE,{"disambiguationData":[OSD([subQ1]),TDD([makeQuery(id+"F10.imprint","IMPRINT",EDGE,{"disambiguationData":[TD([[makeQuery(id+"F10.imprint","INTERSECT",VERTEX,{"derivedFrom":[sQuery(id+"F10.wireOp",EDGE,"E25"),subQ1]}),-1.0]])],"derivedFrom":subQ1})])]})])],"derivedFrom":subQ2});}
            var Q29;
            {var subQ0=sQuery(id+"F0.wireOp",EDGE,"E0");var subQ3=makeQuery(id+"F1.opExtrude","CAP_EDGE",EDGE,{"disambiguationData":[OSD([subQ0])],"isStart":false});var subQ4=sQuery(id+"F0.wireOp",EDGE,"E8");Q29=makeQuery(id+"F11.boolean.opBoolean","SPLIT",EDGE,{"disambiguationData":[TD([makeQuery(id+"F1.opExtrude","SWEPT_FACE",FACE,{"disambiguationData":[OSD([subQ4])]})])],"derivedFrom":subQ3});}
            var Q30;
            {var subQ0=sQuery(id+"F0.wireOp",EDGE,"E0");var subQ1=sQuery(id+"F0.wireOp",EDGE,"E11");var subQ4=makeQuery(id+"F1.opExtrude","CAP_EDGE",EDGE,{"disambiguationData":[OSD([subQ0])],"isStart":false});Q30=makeQuery(id+"F11.boolean.opBoolean","SPLIT",EDGE,{"disambiguationData":[TD([makeQuery(id+"F1.opExtrude","SWEPT_FACE",FACE,{"disambiguationData":[OSD([subQ1])]})])],"derivedFrom":subQ4});}
            var Q31;
            {var subQ0=sQuery(id+"F0.wireOp",EDGE,"E0");var subQ1=sQuery(id+"F10.wireOp",EDGE,"E27");Q31=makeQuery(id+"F11.boolean.opBoolean","SPLIT",EDGE,{"disambiguationData":[TD([makeQuery(id+"F11.opExtrude","SWEPT_FACE",FACE,{"disambiguationData":[OSD([subQ1]),TDD([makeQuery(id+"F10.imprint","IMPRINT",EDGE,{"disambiguationData":[TD([[makeQuery(id+"F10.imprint","INTERSECT",VERTEX,{"derivedFrom":[sQuery(id+"F10.wireOp",EDGE,"E25"),subQ1]}),-1.0]])],"derivedFrom":subQ1})])]})])],"derivedFrom":makeQuery(id+"F1.opExtrude","CAP_EDGE",EDGE,{"disambiguationData":[OSD([subQ0])],"isStart":true})});}
            var Q32;
            {var subQ0=sQuery(id+"F0.wireOp",EDGE,"E0");var subQ1=sQuery(id+"F0.wireOp",EDGE,"E11");Q32=makeQuery(id+"F11.boolean.opBoolean","SPLIT",EDGE,{"disambiguationData":[TD([makeQuery(id+"F1.opExtrude","SWEPT_FACE",FACE,{"disambiguationData":[OSD([subQ1])]})])],"derivedFrom":makeQuery(id+"F1.opExtrude","CAP_EDGE",EDGE,{"disambiguationData":[OSD([subQ0])],"isStart":true})});}
            var Q33;
            {var subQ0=sQuery(id+"F0.wireOp",EDGE,"E0");var subQ3=sQuery(id+"F0.wireOp",EDGE,"E8");Q33=makeQuery(id+"F11.boolean.opBoolean","SPLIT",EDGE,{"disambiguationData":[TD([makeQuery(id+"F1.opExtrude","SWEPT_FACE",FACE,{"disambiguationData":[OSD([subQ3])]})])],"derivedFrom":makeQuery(id+"F1.opExtrude","CAP_EDGE",EDGE,{"disambiguationData":[OSD([subQ0])],"isStart":true})});}
            var Q34;
            Q34=makeQuery(id+"F14.opExtrude","CAP_EDGE",EDGE,{"disambiguationData":[OSD([sQuery(id+"F12.wireOp",EDGE,"E29.left")])],"isStart":false});
            var Q35;
            Q35=makeQuery(id+"F14.opExtrude","CAP_EDGE",EDGE,{"disambiguationData":[OSD([sQuery(id+"F12.wireOp",EDGE,"E29.right")])],"isStart":false});
            var Q36;
            Q36=makeQuery(id+"F14.opExtrude","CAP_EDGE",EDGE,{"disambiguationData":[OSD([sQuery(id+"F13.wireOp",EDGE,"E33")])],"isStart":false});
            var Q37;
            Q37=makeQuery(id+"F14.opExtrude","CAP_EDGE",EDGE,{"disambiguationData":[OSD([sQuery(id+"F13.wireOp",EDGE,"E32")])],"isStart":false});
            fillet(context, id + "F21", {"entities" : qUnion([Q0, Q1, Q2, Q3, Q4, Q5, Q6, Q7, Q8, Q9, Q10, Q11, Q12, Q13, Q14, Q15, Q16, Q17, Q18, Q19, Q20, Q21, Q22, Q23, Q24, Q25, Q26, Q27, Q28, Q29, Q30, Q31, Q32, Q33, Q34, Q35, Q36, Q37]), "radius" : 5.08 * mm, "tangentPropagation" : true, "allowEdgeOverflow" : false});
        }
    });
